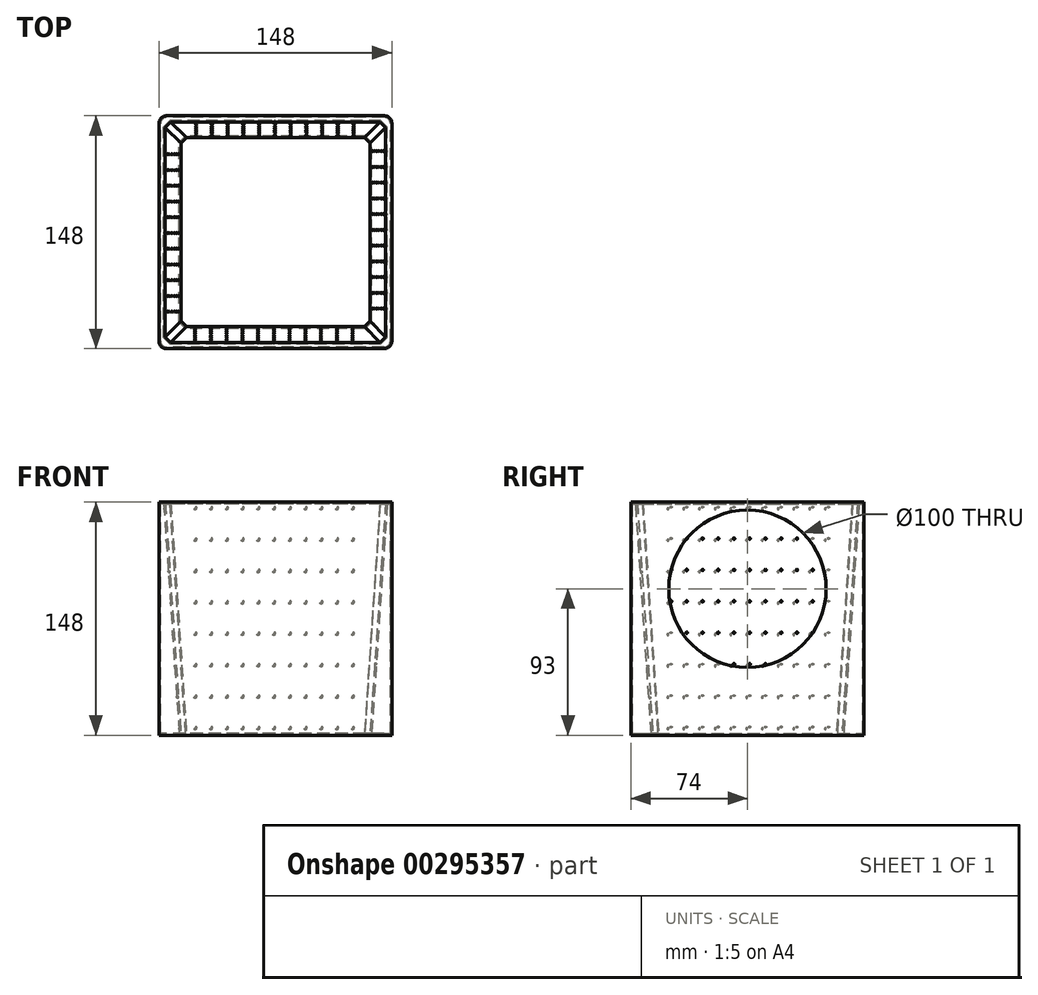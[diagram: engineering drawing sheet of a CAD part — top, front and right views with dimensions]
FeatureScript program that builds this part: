
annotation { "Feature Type Name" : "Feature", "Feature Type Description" : "" }
export const myFeature = defineFeature(function(context is Context, id is Id, definition is map)
    precondition{}
    {
        {
            var Q0;
            Q0=qCreatedBy(makeId("Top.planeOp"),FACE);
            cPlane(context, id + "F0", {"entities" : qUnion([Q0]), "cplaneType" : CPlaneType.OFFSET, "offset" : 148 * mm, "width" : 150 * mm, "height" : 150 * mm});
        }
        {
            var Q0;
            Q0=qCreatedBy(id+"F0.planeOp",FACE);
            var sketch = newSketch(context, id + "F1", { "sketchPlane" : qUnion([Q0])});
            skLineSegment(sketch, "E0.bottom", {"start": v(69, -74) * mm, "end": v(-69, -74) * mm});
            skLineSegment(sketch, "E0.top", {"start": v(69, 74) * mm, "end": v(-69, 74) * mm});
            skLineSegment(sketch, "E0.left", {"start": v(74, -69) * mm, "end": v(74, 69) * mm});
            skLineSegment(sketch, "E0.right", {"start": v(-74, -69) * mm, "end": v(-74, 69) * mm});
            skArc(sketch, "E1.filletArc", {"start": v(74, 69) * mm, "mid": v(72.54, 72.54) * mm, "end": v(69, 74) * mm});
            skArc(sketch, "E2.filletArc", {"start": v(-69, 74) * mm, "mid": v(-72.54, 72.54) * mm, "end": v(-74, 69) * mm});
            skArc(sketch, "E3.filletArc", {"start": v(-74, -69) * mm, "mid": v(-72.54, -72.54) * mm, "end": v(-69, -74) * mm});
            skArc(sketch, "E4.filletArc", {"start": v(69, -74) * mm, "mid": v(72.54, -72.54) * mm, "end": v(74, -69) * mm});
            skSolve(sketch);
        }
        {
            var Q0;
            Q0=qCreatedBy(makeId("Top.planeOp"),FACE);
            var sketch = newSketch(context, id + "F2", { "sketchPlane" : qUnion([Q0])});
            skLineSegment(sketch, "E5.bottom", {"start": v(69, -74) * mm, "end": v(-69, -74) * mm});
            skLineSegment(sketch, "E5.top", {"start": v(69, 74) * mm, "end": v(-69, 74) * mm});
            skLineSegment(sketch, "E5.left", {"start": v(74, -69) * mm, "end": v(74, 69) * mm});
            skLineSegment(sketch, "E5.right", {"start": v(-74, -69) * mm, "end": v(-74, 69) * mm});
            skArc(sketch, "E6.filletArc", {"start": v(69, -74) * mm, "mid": v(72.54, -72.54) * mm, "end": v(74, -69) * mm});
            skArc(sketch, "E7.filletArc", {"start": v(74, 69) * mm, "mid": v(72.54, 72.54) * mm, "end": v(69, 74) * mm});
            skArc(sketch, "E8.filletArc", {"start": v(-69, 74) * mm, "mid": v(-72.54, 72.54) * mm, "end": v(-74, 69) * mm});
            skArc(sketch, "E9.filletArc", {"start": v(-74, -69) * mm, "mid": v(-72.54, -72.54) * mm, "end": v(-69, -74) * mm});
            skSolve(sketch);
        }
        {
            var Q0;
            Q0=qCreatedBy(makeId("Top.planeOp"),FACE);
            var sketch = newSketch(context, id + "F3", { "sketchPlane" : qUnion([Q0])});
            skPoint(sketch, "E10.middle", {"position": v(0, 0) * mm});
            skPoint(sketch, "E11.visualSharp", {"position": v(50, -40) * mm});
            skPoint(sketch, "E12.visualSharp", {"position": v(50, 40) * mm});
            skPoint(sketch, "E13.visualSharp", {"position": v(-50, 40) * mm});
            skLineSegment(sketch, "E14.bottom", {"start": v(56.46, -60) * mm, "end": v(-56.46, -60) * mm});
            skLineSegment(sketch, "E14.top", {"start": v(56.46, 60) * mm, "end": v(-56.46, 60) * mm});
            skLineSegment(sketch, "E14.left", {"start": v(60, -56.46) * mm, "end": v(60, 56.46) * mm});
            skLineSegment(sketch, "E14.right", {"start": v(-60, -56.46) * mm, "end": v(-60, 56.46) * mm});
            skPoint(sketch, "E15.visualSharp", {"position": v(60, -60) * mm});
            skPoint(sketch, "E16.visualSharp", {"position": v(60, 60) * mm});
            skPoint(sketch, "E17.visualSharp", {"position": v(-60, 60) * mm});
            skLineSegment(sketch, "E18", {"start": v(-60, 56.46) * mm, "end": v(-56.46, 60) * mm});
            skLineSegment(sketch, "E19", {"start": v(-60, -56.46) * mm, "end": v(-56.46, -60) * mm});
            skLineSegment(sketch, "E20", {"start": v(56.46, -60) * mm, "end": v(60, -56.46) * mm});
            skLineSegment(sketch, "E21", {"start": v(60, 56.46) * mm, "end": v(56.46, 60) * mm});
            skSolve(sketch);
        }
        {
            var Q0;
            Q0=makeQuery(id+"F1.imprint","IMPRINT",FACE,{"disambiguationData":[TD([[makeQuery(id+"F1.imprint","IMPRINT",EDGE,{"derivedFrom":sQuery(id+"F1.wireOp",EDGE,"E0.bottom")}),-1.0]])]});
            var sketch = newSketch(context, id + "F4", { "sketchPlane" : qUnion([Q0])});
            skPoint(sketch, "E22.middle", {"position": v(0, 0) * mm});
            skPoint(sketch, "E23.visualSharp", {"position": v(75, 75) * mm});
            skPoint(sketch, "E24.visualSharp", {"position": v(-75, 75) * mm});
            skPoint(sketch, "E25.visualSharp", {"position": v(-75, -75) * mm});
            skPoint(sketch, "E26.visualSharp", {"position": v(75, -75) * mm});
            skLineSegment(sketch, "E27.bottom", {"start": v(66.46, -70) * mm, "end": v(-66.46, -70) * mm});
            skLineSegment(sketch, "E27.top", {"start": v(66.46, 70) * mm, "end": v(-66.46, 70) * mm});
            skLineSegment(sketch, "E27.left", {"start": v(70, -66.46) * mm, "end": v(70, 66.46) * mm});
            skLineSegment(sketch, "E27.right", {"start": v(-70, -66.46) * mm, "end": v(-70, 66.46) * mm});
            skPoint(sketch, "E28.visualSharp", {"position": v(70, 70) * mm});
            skPoint(sketch, "E29.visualSharp", {"position": v(70, -70) * mm});
            skPoint(sketch, "E30.visualSharp", {"position": v(-70, -70) * mm});
            skPoint(sketch, "E31.visualSharp", {"position": v(-70, 70) * mm});
            skLineSegment(sketch, "E32", {"start": v(-70, 66.46) * mm, "end": v(-66.46, 70) * mm});
            skLineSegment(sketch, "E33", {"start": v(-70, -66.46) * mm, "end": v(-66.46, -70) * mm});
            skLineSegment(sketch, "E34", {"start": v(66.46, -70) * mm, "end": v(70, -66.46) * mm});
            skLineSegment(sketch, "E35", {"start": v(70, 66.46) * mm, "end": v(66.46, 70) * mm});
            skSolve(sketch);
        }
        {
            var Q0;
            Q0=makeQuery(id+"F1.imprint","IMPRINT",FACE,{"disambiguationData":[TD([[makeQuery(id+"F1.imprint","IMPRINT",EDGE,{"derivedFrom":sQuery(id+"F1.wireOp",EDGE,"E0.bottom")}),-1.0]])]});
            var Q1;
            Q1=makeQuery(id+"F2.imprint","IMPRINT",FACE,{"disambiguationData":[TD([[makeQuery(id+"F2.imprint","IMPRINT",EDGE,{"derivedFrom":sQuery(id+"F2.wireOp",EDGE,"E5.bottom")}),-1.0]])]});
            loft(context, id + "F5", {"sheetProfilesArray" : [{ "sheetProfileEntities" : qUnion([Q0]) }, { "sheetProfileEntities" : qUnion([Q1]) }]});
        }
        {
            var Q1;
            Q1=makeQuery(id+"F4.imprint","IMPRINT",FACE,{"disambiguationData":[TD([[makeQuery(id+"F4.imprint","IMPRINT",EDGE,{"derivedFrom":sQuery(id+"F4.wireOp",EDGE,"E27.bottom")}),-1.0]])]});
            var Q2;
            Q2=makeQuery(id+"F3.imprint","IMPRINT",FACE,{"disambiguationData":[TD([[makeQuery(id+"F3.imprint","IMPRINT",EDGE,{"derivedFrom":sQuery(id+"F3.wireOp",EDGE,"E14.bottom")}),-1.0]])]});
            loft(context, id + "F6", {"operationType" : NewBodyOperationType.REMOVE, "sheetProfilesArray" : [{ "sheetProfileEntities" : qUnion([Q1]) }, { "sheetProfileEntities" : qUnion([Q2]) }]});
        }
        {
            var Q0;
            Q0=makeQuery(id+"F5.opLoft","CAP_FACE",FACE,{"disambiguationData":[OSD([makeQuery(id+"F1.imprint","IMPRINT",FACE,{"disambiguationData":[TD([[makeQuery(id+"F1.imprint","IMPRINT",EDGE,{"derivedFrom":sQuery(id+"F1.wireOp",EDGE,"E0.bottom")}),-1.0]])]})])],"isStart":true});
            var Q1;
            Q1=makeQuery(id+"F5.opLoft","SWEPT_BODY",BODY,{"disambiguationData":[OSD([makeQuery(id+"F1.imprint","IMPRINT",FACE,{"disambiguationData":[TD([[makeQuery(id+"F1.imprint","IMPRINT",EDGE,{"derivedFrom":sQuery(id+"F1.wireOp",EDGE,"E0.bottom")}),-1.0]])]}),makeQuery(id+"F2.imprint","IMPRINT",FACE,{"disambiguationData":[TD([[makeQuery(id+"F2.imprint","IMPRINT",EDGE,{"derivedFrom":sQuery(id+"F2.wireOp",EDGE,"E5.bottom")}),-1.0]])]})])]});
            shell(context, id + "F7", {"isHollow" : true, "entities" : qUnion([Q0]), "parts" : qUnion([Q1]), "thickness" : 1 * mm});
        }
        {
            var Q0;
            Q0=makeQuery(id+"F6.boolean.opBoolean","COPY",FACE,{"derivedFrom":makeQuery(id+"F6.opLoft","SWEPT_FACE",FACE,{"disambiguationData":[OSD([sQuery(id+"F3.wireOp",EDGE,"E14.top"),sQuery(id+"F3.wireOp",EDGE,"E16.filletArc"),sQuery(id+"F3.wireOp",EDGE,"E17.filletArc"),sQuery(id+"F4.wireOp",EDGE,"E27.top"),sQuery(id+"F4.wireOp",EDGE,"E28.filletArc"),sQuery(id+"F4.wireOp",EDGE,"E31.filletArc")])]})});
            var sketch = newSketch(context, id + "F8", { "sketchPlane" : qUnion([Q0])});
            skPoint(sketch, "E36", {"position": v(-50.4, 148.96) * mm});
            skPoint(sketch, "E37.0.1.0", {"position": v(-50.4, 128.96) * mm});
            skPoint(sketch, "E37.0.2.0", {"position": v(-50.4, 108.96) * mm});
            skPoint(sketch, "E37.0.3.0", {"position": v(-50.4, 88.96) * mm});
            skPoint(sketch, "E37.0.4.0", {"position": v(-50.4, 68.96) * mm});
            skPoint(sketch, "E37.1.0.0", {"position": v(-40.4, 148.96) * mm});
            skPoint(sketch, "E37.1.1.0", {"position": v(-40.4, 128.96) * mm});
            skPoint(sketch, "E37.1.2.0", {"position": v(-40.4, 108.96) * mm});
            skPoint(sketch, "E37.1.3.0", {"position": v(-40.4, 88.96) * mm});
            skPoint(sketch, "E37.1.4.0", {"position": v(-40.4, 68.96) * mm});
            skPoint(sketch, "E37.2.0.0", {"position": v(-30.4, 148.96) * mm});
            skPoint(sketch, "E37.2.1.0", {"position": v(-30.4, 128.96) * mm});
            skPoint(sketch, "E37.2.2.0", {"position": v(-30.4, 108.96) * mm});
            skPoint(sketch, "E37.2.3.0", {"position": v(-30.4, 88.96) * mm});
            skPoint(sketch, "E37.2.4.0", {"position": v(-30.4, 68.96) * mm});
            skPoint(sketch, "E37.3.0.0", {"position": v(-20.4, 148.96) * mm});
            skPoint(sketch, "E37.3.1.0", {"position": v(-20.4, 128.96) * mm});
            skPoint(sketch, "E37.3.2.0", {"position": v(-20.4, 108.96) * mm});
            skPoint(sketch, "E37.3.3.0", {"position": v(-20.4, 88.96) * mm});
            skPoint(sketch, "E37.3.4.0", {"position": v(-20.4, 68.96) * mm});
            skPoint(sketch, "E37.4.0.0", {"position": v(-10.4, 148.96) * mm});
            skPoint(sketch, "E37.4.1.0", {"position": v(-10.4, 128.96) * mm});
            skPoint(sketch, "E37.4.2.0", {"position": v(-10.4, 108.96) * mm});
            skPoint(sketch, "E37.4.3.0", {"position": v(-10.4, 88.96) * mm});
            skPoint(sketch, "E37.4.4.0", {"position": v(-10.4, 68.96) * mm});
            skPoint(sketch, "E37.5.0.0", {"position": v(-0.4, 148.96) * mm});
            skPoint(sketch, "E37.5.1.0", {"position": v(-0.4, 128.96) * mm});
            skPoint(sketch, "E37.5.2.0", {"position": v(-0.4, 108.96) * mm});
            skPoint(sketch, "E37.5.3.0", {"position": v(-0.4, 88.96) * mm});
            skPoint(sketch, "E37.5.4.0", {"position": v(-0.4, 68.96) * mm});
            skPoint(sketch, "E37.6.0.0", {"position": v(9.6, 148.96) * mm});
            skPoint(sketch, "E37.6.1.0", {"position": v(9.6, 128.96) * mm});
            skPoint(sketch, "E37.6.2.0", {"position": v(9.6, 108.96) * mm});
            skPoint(sketch, "E37.6.3.0", {"position": v(9.6, 88.96) * mm});
            skPoint(sketch, "E37.6.4.0", {"position": v(9.6, 68.96) * mm});
            skPoint(sketch, "E37.7.0.0", {"position": v(19.6, 148.96) * mm});
            skPoint(sketch, "E37.7.1.0", {"position": v(19.6, 128.96) * mm});
            skPoint(sketch, "E37.7.2.0", {"position": v(19.6, 108.96) * mm});
            skPoint(sketch, "E37.7.3.0", {"position": v(19.6, 88.96) * mm});
            skPoint(sketch, "E37.7.4.0", {"position": v(19.6, 68.96) * mm});
            skPoint(sketch, "E37.8.0.0", {"position": v(29.6, 148.96) * mm});
            skPoint(sketch, "E37.8.1.0", {"position": v(29.6, 128.96) * mm});
            skPoint(sketch, "E37.8.2.0", {"position": v(29.6, 108.96) * mm});
            skPoint(sketch, "E37.8.3.0", {"position": v(29.6, 88.96) * mm});
            skPoint(sketch, "E37.8.4.0", {"position": v(29.6, 68.96) * mm});
            skPoint(sketch, "E37.9.0.0", {"position": v(39.6, 148.96) * mm});
            skPoint(sketch, "E37.9.1.0", {"position": v(39.6, 128.96) * mm});
            skPoint(sketch, "E37.9.2.0", {"position": v(39.6, 108.96) * mm});
            skPoint(sketch, "E37.9.3.0", {"position": v(39.6, 88.96) * mm});
            skPoint(sketch, "E37.9.4.0", {"position": v(39.6, 68.96) * mm});
            skLineSegment(sketch, "E37.direction1", {"start": v(-50.4, 148.96) * mm, "end": v(-40.4, 148.96) * mm, "construction": true});
            skLineSegment(sketch, "E37.direction2", {"start": v(-50.4, 148.96) * mm, "end": v(-50.4, 128.96) * mm, "construction": true});
            skPoint(sketch, "E38.0.0.5", {"position": v(-50.4, 48.96) * mm});
            skPoint(sketch, "E38.0.0.6", {"position": v(-50.4, 28.96) * mm});
            skPoint(sketch, "E38.0.0.7", {"position": v(-50.4, 8.96) * mm});
            skPoint(sketch, "E38.0.1.5", {"position": v(-40.4, 48.96) * mm});
            skPoint(sketch, "E38.0.1.6", {"position": v(-40.4, 28.96) * mm});
            skPoint(sketch, "E38.0.1.7", {"position": v(-40.4, 8.96) * mm});
            skPoint(sketch, "E38.0.2.5", {"position": v(-30.4, 48.96) * mm});
            skPoint(sketch, "E38.0.2.6", {"position": v(-30.4, 28.96) * mm});
            skPoint(sketch, "E38.0.2.7", {"position": v(-30.4, 8.96) * mm});
            skPoint(sketch, "E38.0.3.5", {"position": v(-20.4, 48.96) * mm});
            skPoint(sketch, "E38.0.3.6", {"position": v(-20.4, 28.96) * mm});
            skPoint(sketch, "E38.0.3.7", {"position": v(-20.4, 8.96) * mm});
            skPoint(sketch, "E38.0.4.5", {"position": v(-10.4, 48.96) * mm});
            skPoint(sketch, "E38.0.4.6", {"position": v(-10.4, 28.96) * mm});
            skPoint(sketch, "E38.0.4.7", {"position": v(-10.4, 8.96) * mm});
            skPoint(sketch, "E38.0.5.5", {"position": v(-0.4, 48.96) * mm});
            skPoint(sketch, "E38.0.5.6", {"position": v(-0.4, 28.96) * mm});
            skPoint(sketch, "E38.0.5.7", {"position": v(-0.4, 8.96) * mm});
            skPoint(sketch, "E38.0.6.5", {"position": v(9.6, 48.96) * mm});
            skPoint(sketch, "E38.0.6.6", {"position": v(9.6, 28.96) * mm});
            skPoint(sketch, "E38.0.6.7", {"position": v(9.6, 8.96) * mm});
            skPoint(sketch, "E38.0.7.5", {"position": v(19.6, 48.96) * mm});
            skPoint(sketch, "E38.0.7.6", {"position": v(19.6, 28.96) * mm});
            skPoint(sketch, "E38.0.7.7", {"position": v(19.6, 8.96) * mm});
            skPoint(sketch, "E38.0.8.5", {"position": v(29.6, 48.96) * mm});
            skPoint(sketch, "E38.0.8.6", {"position": v(29.6, 28.96) * mm});
            skPoint(sketch, "E38.0.8.7", {"position": v(29.6, 8.96) * mm});
            skPoint(sketch, "E38.0.9.5", {"position": v(39.6, 48.96) * mm});
            skPoint(sketch, "E38.0.9.6", {"position": v(39.6, 28.96) * mm});
            skPoint(sketch, "E38.0.9.7", {"position": v(39.6, 8.96) * mm});
            skPoint(sketch, "E39.0.10.0", {"position": v(49.6, 148.96) * mm});
            skPoint(sketch, "E39.0.10.1", {"position": v(49.6, 128.96) * mm});
            skPoint(sketch, "E39.0.10.2", {"position": v(49.6, 108.96) * mm});
            skPoint(sketch, "E39.0.10.3", {"position": v(49.6, 88.96) * mm});
            skPoint(sketch, "E39.0.10.4", {"position": v(49.6, 68.96) * mm});
            skPoint(sketch, "E39.0.10.5", {"position": v(49.6, 48.96) * mm});
            skPoint(sketch, "E39.0.10.6", {"position": v(49.6, 28.96) * mm});
            skPoint(sketch, "E39.0.10.7", {"position": v(49.6, 8.96) * mm});
            skSolve(sketch);
        }
        {
            var Q0;
            Q0=sQuery(id+"F8.wireOp",VERTEX,"E36");
            var Q1;
            Q1=sQuery(id+"F8.wireOp",VERTEX,"E37.3.0.0");
            var Q2;
            Q2=sQuery(id+"F8.wireOp",VERTEX,"E37.6.1.0");
            var Q3;
            Q3=sQuery(id+"F8.wireOp",VERTEX,"E37.3.2.0");
            var Q4;
            Q4=sQuery(id+"F8.wireOp",VERTEX,"E37.6.3.0");
            var Q5;
            Q5=sQuery(id+"F8.wireOp",VERTEX,"E37.5.1.0");
            var Q6;
            Q6=sQuery(id+"F8.wireOp",VERTEX,"E37.8.2.0");
            var Q7;
            Q7=sQuery(id+"F8.wireOp",VERTEX,"E37.4.1.0");
            var Q8;
            Q8=sQuery(id+"F8.wireOp",VERTEX,"E37.7.4.0");
            var Q9;
            Q9=sQuery(id+"F8.wireOp",VERTEX,"E37.4.3.0");
            var Q10;
            Q10=sQuery(id+"F8.wireOp",VERTEX,"E37.2.2.0");
            var Q11;
            Q11=sQuery(id+"F8.wireOp",VERTEX,"E37.5.3.0");
            var Q12;
            Q12=sQuery(id+"F8.wireOp",VERTEX,"E37.2.4.0");
            var Q13;
            Q13=sQuery(id+"F8.wireOp",VERTEX,"E37.6.0.0");
            var Q14;
            Q14=sQuery(id+"F8.wireOp",VERTEX,"E37.7.0.0");
            var Q15;
            Q15=sQuery(id+"F8.wireOp",VERTEX,"E37.3.4.0");
            var Q16;
            Q16=sQuery(id+"F8.wireOp",VERTEX,"E37.7.2.0");
            var Q17;
            Q17=sQuery(id+"F8.wireOp",VERTEX,"E37.3.1.0");
            var Q18;
            Q18=sQuery(id+"F8.wireOp",VERTEX,"E37.5.0.0");
            var Q19;
            Q19=sQuery(id+"F8.wireOp",VERTEX,"E37.6.2.0");
            var Q20;
            Q20=sQuery(id+"F8.wireOp",VERTEX,"E37.8.1.0");
            var Q21;
            Q21=sQuery(id+"F8.wireOp",VERTEX,"E37.3.3.0");
            var Q22;
            Q22=sQuery(id+"F8.wireOp",VERTEX,"E37.6.4.0");
            var Q23;
            Q23=sQuery(id+"F8.wireOp",VERTEX,"E37.5.2.0");
            var Q24;
            Q24=sQuery(id+"F8.wireOp",VERTEX,"E37.1.2.0");
            var Q25;
            Q25=sQuery(id+"F8.wireOp",VERTEX,"E37.1.1.0");
            var Q26;
            Q26=sQuery(id+"F8.wireOp",VERTEX,"E37.1.0.0");
            var Q27;
            Q27=sQuery(id+"F8.wireOp",VERTEX,"E37.7.3.0");
            var Q28;
            Q28=sQuery(id+"F8.wireOp",VERTEX,"E37.4.2.0");
            var Q29;
            Q29=sQuery(id+"F8.wireOp",VERTEX,"E37.8.0.0");
            var Q30;
            Q30=sQuery(id+"F8.wireOp",VERTEX,"E37.4.4.0");
            var Q31;
            Q31=sQuery(id+"F8.wireOp",VERTEX,"E37.2.3.0");
            var Q32;
            Q32=sQuery(id+"F8.wireOp",VERTEX,"E37.5.4.0");
            var Q33;
            Q33=sQuery(id+"F8.wireOp",VERTEX,"E37.9.0.0");
            var Q34;
            Q34=sQuery(id+"F8.wireOp",VERTEX,"E37.2.1.0");
            var Q35;
            Q35=sQuery(id+"F8.wireOp",VERTEX,"E37.2.0.0");
            var Q36;
            Q36=sQuery(id+"F8.wireOp",VERTEX,"E37.7.1.0");
            var Q37;
            Q37=sQuery(id+"F8.wireOp",VERTEX,"E37.4.0.0");
            var Q38;
            Q38=sQuery(id+"F8.wireOp",VERTEX,"E37.9.4.0");
            var Q39;
            Q39=sQuery(id+"F8.wireOp",VERTEX,"E39.0.10.6");
            var Q40;
            Q40=sQuery(id+"F8.wireOp",VERTEX,"E39.0.10.3");
            var Q41;
            Q41=sQuery(id+"F8.wireOp",VERTEX,"E38.0.5.6");
            var Q42;
            Q42=sQuery(id+"F8.wireOp",VERTEX,"E38.0.8.6");
            var Q43;
            Q43=sQuery(id+"F8.wireOp",VERTEX,"E38.0.9.6");
            var Q44;
            Q44=sQuery(id+"F8.wireOp",VERTEX,"E38.0.0.6");
            var Q45;
            Q45=sQuery(id+"F8.wireOp",VERTEX,"E39.0.10.5");
            var Q46;
            Q46=sQuery(id+"F8.wireOp",VERTEX,"E38.0.4.7");
            var Q47;
            Q47=sQuery(id+"F8.wireOp",VERTEX,"E38.0.7.5");
            var Q48;
            Q48=sQuery(id+"F8.wireOp",VERTEX,"E38.0.5.7");
            var Q49;
            Q49=sQuery(id+"F8.wireOp",VERTEX,"E38.0.8.7");
            var Q50;
            Q50=sQuery(id+"F8.wireOp",VERTEX,"E38.0.3.6");
            var Q51;
            Q51=sQuery(id+"F8.wireOp",VERTEX,"E39.0.10.2");
            var Q52;
            Q52=sQuery(id+"F8.wireOp",VERTEX,"E37.0.3.0");
            var Q53;
            Q53=sQuery(id+"F8.wireOp",VERTEX,"E37.9.3.0");
            var Q54;
            Q54=sQuery(id+"F8.wireOp",VERTEX,"E39.0.10.0");
            var Q55;
            Q55=sQuery(id+"F8.wireOp",VERTEX,"E38.0.9.5");
            var Q56;
            Q56=sQuery(id+"F8.wireOp",VERTEX,"E38.0.7.6");
            var Q57;
            Q57=sQuery(id+"F8.wireOp",VERTEX,"E38.0.7.7");
            var Q58;
            Q58=sQuery(id+"F8.wireOp",VERTEX,"E38.0.3.7");
            var Q59;
            Q59=sQuery(id+"F8.wireOp",VERTEX,"E37.9.1.0");
            var Q60;
            Q60=sQuery(id+"F8.wireOp",VERTEX,"E38.0.0.5");
            var Q61;
            Q61=sQuery(id+"F8.wireOp",VERTEX,"E39.0.10.1");
            var Q62;
            Q62=sQuery(id+"F8.wireOp",VERTEX,"E38.0.2.7");
            var Q63;
            Q63=sQuery(id+"F8.wireOp",VERTEX,"E37.0.2.0");
            var Q64;
            Q64=sQuery(id+"F8.wireOp",VERTEX,"E37.0.1.0");
            var Q65;
            Q65=sQuery(id+"F8.wireOp",VERTEX,"E39.0.10.7");
            var Q66;
            Q66=sQuery(id+"F8.wireOp",VERTEX,"E37.1.4.0");
            var Q67;
            Q67=sQuery(id+"F8.wireOp",VERTEX,"E38.0.8.5");
            var Q68;
            Q68=sQuery(id+"F8.wireOp",VERTEX,"E38.0.5.5");
            var Q69;
            Q69=sQuery(id+"F8.wireOp",VERTEX,"E37.9.2.0");
            var Q70;
            Q70=sQuery(id+"F8.wireOp",VERTEX,"E38.0.4.6");
            var Q71;
            Q71=sQuery(id+"F8.wireOp",VERTEX,"E37.8.3.0");
            var Q72;
            Q72=sQuery(id+"F8.wireOp",VERTEX,"E37.0.4.0");
            var Q73;
            Q73=sQuery(id+"F8.wireOp",VERTEX,"E38.0.0.7");
            var Q74;
            Q74=sQuery(id+"F8.wireOp",VERTEX,"E39.0.10.4");
            var Q75;
            Q75=sQuery(id+"F8.wireOp",VERTEX,"E38.0.1.6");
            var Q76;
            Q76=sQuery(id+"F8.wireOp",VERTEX,"E38.0.9.7");
            var Q77;
            Q77=sQuery(id+"F8.wireOp",VERTEX,"E37.8.4.0");
            var Q78;
            Q78=sQuery(id+"F8.wireOp",VERTEX,"E38.0.2.6");
            var Q79;
            Q79=sQuery(id+"F8.wireOp",VERTEX,"E37.1.3.0");
            var Q80;
            Q80=sQuery(id+"F8.wireOp",VERTEX,"E38.0.3.5");
            var Q81;
            Q81=sQuery(id+"F8.wireOp",VERTEX,"E38.0.1.5");
            var Q82;
            Q82=sQuery(id+"F8.wireOp",VERTEX,"E38.0.6.6");
            var Q83;
            Q83=sQuery(id+"F8.wireOp",VERTEX,"E38.0.1.7");
            var Q84;
            Q84=sQuery(id+"F8.wireOp",VERTEX,"E38.0.6.5");
            var Q85;
            Q85=sQuery(id+"F8.wireOp",VERTEX,"E38.0.4.5");
            var Q86;
            Q86=sQuery(id+"F8.wireOp",VERTEX,"E38.0.6.7");
            var Q87;
            Q87=sQuery(id+"F8.wireOp",VERTEX,"E38.0.2.5");
            var Q88;
            Q88=makeQuery(id+"F5.opLoft","SWEPT_BODY",BODY,{"disambiguationData":[OSD([makeQuery(id+"F1.imprint","IMPRINT",FACE,{"disambiguationData":[TD([[makeQuery(id+"F1.imprint","IMPRINT",EDGE,{"derivedFrom":sQuery(id+"F1.wireOp",EDGE,"E0.bottom")}),-1.0]])]}),makeQuery(id+"F2.imprint","IMPRINT",FACE,{"disambiguationData":[TD([[makeQuery(id+"F2.imprint","IMPRINT",EDGE,{"derivedFrom":sQuery(id+"F2.wireOp",EDGE,"E5.bottom")}),-1.0]])]})])]});
            hole(context, id + "F9", {"style" : HoleStyle.SIMPLE, "endStyle" : HoleEndStyle.BLIND, "holeDiameter" : 1 * mm, "holeDepth" : 1 * mm, "tappedDepth" : 12 * mm, "tapClearance" : 3, "locations" : qUnion([Q0, Q1, Q2, Q3, Q4, Q5, Q6, Q7, Q8, Q9, Q10, Q11, Q12, Q13, Q14, Q15, Q16, Q17, Q18, Q19, Q20, Q21, Q22, Q23, Q24, Q25, Q26, Q27, Q28, Q29, Q30, Q31, Q32, Q33, Q34, Q35, Q36, Q37, Q38, Q39, Q40, Q41, Q42, Q43, Q44, Q45, Q46, Q47, Q48, Q49, Q50, Q51, Q52, Q53, Q54, Q55, Q56, Q57, Q58, Q59, Q60, Q61, Q62, Q63, Q64, Q65, Q66, Q67, Q68, Q69, Q70, Q71, Q72, Q73, Q74, Q75, Q76, Q77, Q78, Q79, Q80, Q81, Q82, Q83, Q84, Q85, Q86, Q87]), "scope" : qUnion([Q88])});
        }
        {
            var Q0;
            Q0=makeQuery(id+"F6.boolean.opBoolean","COPY",FACE,{"derivedFrom":makeQuery(id+"F6.opLoft","SWEPT_FACE",FACE,{"disambiguationData":[OSD([sQuery(id+"F3.wireOp",EDGE,"E14.right"),sQuery(id+"F3.wireOp",EDGE,"E18"),sQuery(id+"F3.wireOp",EDGE,"E19"),sQuery(id+"F4.wireOp",EDGE,"E27.right"),sQuery(id+"F4.wireOp",EDGE,"E32"),sQuery(id+"F4.wireOp",EDGE,"E33")])]})});
            var sketch = newSketch(context, id + "F10", { "sketchPlane" : qUnion([Q0])});
            skPoint(sketch, "E40", {"position": v(-50.5, 148.2) * mm});
            skPoint(sketch, "E41.0.1.0", {"position": v(-50.5, 128.2) * mm});
            skPoint(sketch, "E41.0.2.0", {"position": v(-50.5, 108.2) * mm});
            skPoint(sketch, "E41.0.3.0", {"position": v(-50.5, 88.2) * mm});
            skPoint(sketch, "E41.0.4.0", {"position": v(-50.5, 68.2) * mm});
            skPoint(sketch, "E41.1.0.0", {"position": v(-40.5, 148.2) * mm});
            skPoint(sketch, "E41.1.1.0", {"position": v(-40.5, 128.2) * mm});
            skPoint(sketch, "E41.1.2.0", {"position": v(-40.5, 108.2) * mm});
            skPoint(sketch, "E41.1.3.0", {"position": v(-40.5, 88.2) * mm});
            skPoint(sketch, "E41.1.4.0", {"position": v(-40.5, 68.2) * mm});
            skPoint(sketch, "E41.2.0.0", {"position": v(-30.5, 148.2) * mm});
            skPoint(sketch, "E41.2.1.0", {"position": v(-30.5, 128.2) * mm});
            skPoint(sketch, "E41.2.2.0", {"position": v(-30.5, 108.2) * mm});
            skPoint(sketch, "E41.2.3.0", {"position": v(-30.5, 88.2) * mm});
            skPoint(sketch, "E41.2.4.0", {"position": v(-30.5, 68.2) * mm});
            skPoint(sketch, "E41.3.0.0", {"position": v(-20.5, 148.2) * mm});
            skPoint(sketch, "E41.3.1.0", {"position": v(-20.5, 128.2) * mm});
            skPoint(sketch, "E41.3.2.0", {"position": v(-20.5, 108.2) * mm});
            skPoint(sketch, "E41.3.3.0", {"position": v(-20.5, 88.2) * mm});
            skPoint(sketch, "E41.3.4.0", {"position": v(-20.5, 68.2) * mm});
            skPoint(sketch, "E41.4.0.0", {"position": v(-10.5, 148.2) * mm});
            skPoint(sketch, "E41.4.1.0", {"position": v(-10.5, 128.2) * mm});
            skPoint(sketch, "E41.4.2.0", {"position": v(-10.5, 108.2) * mm});
            skPoint(sketch, "E41.4.3.0", {"position": v(-10.5, 88.2) * mm});
            skPoint(sketch, "E41.4.4.0", {"position": v(-10.5, 68.2) * mm});
            skPoint(sketch, "E41.5.0.0", {"position": v(-0.5, 148.2) * mm});
            skPoint(sketch, "E41.5.1.0", {"position": v(-0.5, 128.2) * mm});
            skPoint(sketch, "E41.5.2.0", {"position": v(-0.5, 108.2) * mm});
            skPoint(sketch, "E41.5.3.0", {"position": v(-0.5, 88.2) * mm});
            skPoint(sketch, "E41.5.4.0", {"position": v(-0.5, 68.2) * mm});
            skPoint(sketch, "E41.6.0.0", {"position": v(9.5, 148.2) * mm});
            skPoint(sketch, "E41.6.1.0", {"position": v(9.5, 128.2) * mm});
            skPoint(sketch, "E41.6.2.0", {"position": v(9.5, 108.2) * mm});
            skPoint(sketch, "E41.6.3.0", {"position": v(9.5, 88.2) * mm});
            skPoint(sketch, "E41.6.4.0", {"position": v(9.5, 68.2) * mm});
            skPoint(sketch, "E41.7.0.0", {"position": v(19.5, 148.2) * mm});
            skPoint(sketch, "E41.7.1.0", {"position": v(19.5, 128.2) * mm});
            skPoint(sketch, "E41.7.2.0", {"position": v(19.5, 108.2) * mm});
            skPoint(sketch, "E41.7.3.0", {"position": v(19.5, 88.2) * mm});
            skPoint(sketch, "E41.7.4.0", {"position": v(19.5, 68.2) * mm});
            skPoint(sketch, "E41.8.0.0", {"position": v(29.5, 148.2) * mm});
            skPoint(sketch, "E41.8.1.0", {"position": v(29.5, 128.2) * mm});
            skPoint(sketch, "E41.8.2.0", {"position": v(29.5, 108.2) * mm});
            skPoint(sketch, "E41.8.3.0", {"position": v(29.5, 88.2) * mm});
            skPoint(sketch, "E41.8.4.0", {"position": v(29.5, 68.2) * mm});
            skPoint(sketch, "E41.9.0.0", {"position": v(39.5, 148.2) * mm});
            skPoint(sketch, "E41.9.1.0", {"position": v(39.5, 128.2) * mm});
            skPoint(sketch, "E41.9.2.0", {"position": v(39.5, 108.2) * mm});
            skPoint(sketch, "E41.9.3.0", {"position": v(39.5, 88.2) * mm});
            skPoint(sketch, "E41.9.4.0", {"position": v(39.5, 68.2) * mm});
            skLineSegment(sketch, "E41.direction1", {"start": v(-50.5, 148.2) * mm, "end": v(-40.5, 148.2) * mm, "construction": true});
            skLineSegment(sketch, "E41.direction2", {"start": v(-50.5, 148.2) * mm, "end": v(-50.5, 128.2) * mm, "construction": true});
            skPoint(sketch, "E42.0.0.5", {"position": v(-50.5, 48.2) * mm});
            skPoint(sketch, "E42.0.0.6", {"position": v(-50.5, 28.2) * mm});
            skPoint(sketch, "E42.0.0.7", {"position": v(-50.5, 8.2) * mm});
            skPoint(sketch, "E42.0.1.5", {"position": v(-40.5, 48.2) * mm});
            skPoint(sketch, "E42.0.1.6", {"position": v(-40.5, 28.2) * mm});
            skPoint(sketch, "E42.0.1.7", {"position": v(-40.5, 8.2) * mm});
            skPoint(sketch, "E42.0.2.5", {"position": v(-30.5, 48.2) * mm});
            skPoint(sketch, "E42.0.2.6", {"position": v(-30.5, 28.2) * mm});
            skPoint(sketch, "E42.0.2.7", {"position": v(-30.5, 8.2) * mm});
            skPoint(sketch, "E42.0.3.5", {"position": v(-20.5, 48.2) * mm});
            skPoint(sketch, "E42.0.3.6", {"position": v(-20.5, 28.2) * mm});
            skPoint(sketch, "E42.0.3.7", {"position": v(-20.5, 8.2) * mm});
            skPoint(sketch, "E42.0.4.5", {"position": v(-10.5, 48.2) * mm});
            skPoint(sketch, "E42.0.4.6", {"position": v(-10.5, 28.2) * mm});
            skPoint(sketch, "E42.0.4.7", {"position": v(-10.5, 8.2) * mm});
            skPoint(sketch, "E42.0.5.5", {"position": v(-0.5, 48.2) * mm});
            skPoint(sketch, "E42.0.5.6", {"position": v(-0.5, 28.2) * mm});
            skPoint(sketch, "E42.0.5.7", {"position": v(-0.5, 8.2) * mm});
            skPoint(sketch, "E42.0.6.5", {"position": v(9.5, 48.2) * mm});
            skPoint(sketch, "E42.0.6.6", {"position": v(9.5, 28.2) * mm});
            skPoint(sketch, "E42.0.6.7", {"position": v(9.5, 8.2) * mm});
            skPoint(sketch, "E42.0.7.5", {"position": v(19.5, 48.2) * mm});
            skPoint(sketch, "E42.0.7.6", {"position": v(19.5, 28.2) * mm});
            skPoint(sketch, "E42.0.7.7", {"position": v(19.5, 8.2) * mm});
            skPoint(sketch, "E42.0.8.5", {"position": v(29.5, 48.2) * mm});
            skPoint(sketch, "E42.0.8.6", {"position": v(29.5, 28.2) * mm});
            skPoint(sketch, "E42.0.8.7", {"position": v(29.5, 8.2) * mm});
            skPoint(sketch, "E42.0.9.5", {"position": v(39.5, 48.2) * mm});
            skPoint(sketch, "E42.0.9.6", {"position": v(39.5, 28.2) * mm});
            skPoint(sketch, "E42.0.9.7", {"position": v(39.5, 8.2) * mm});
            skPoint(sketch, "E43.0.10.0", {"position": v(49.5, 148.2) * mm});
            skPoint(sketch, "E43.0.10.1", {"position": v(49.5, 128.2) * mm});
            skPoint(sketch, "E43.0.10.2", {"position": v(49.5, 108.2) * mm});
            skPoint(sketch, "E43.0.10.3", {"position": v(49.5, 88.2) * mm});
            skPoint(sketch, "E43.0.10.4", {"position": v(49.5, 68.2) * mm});
            skPoint(sketch, "E43.0.10.5", {"position": v(49.5, 48.2) * mm});
            skPoint(sketch, "E43.0.10.6", {"position": v(49.5, 28.2) * mm});
            skPoint(sketch, "E43.0.10.7", {"position": v(49.5, 8.2) * mm});
            skSolve(sketch);
        }
        {
            var Q0;
            Q0=makeQuery(id+"F6.boolean.opBoolean","COPY",FACE,{"derivedFrom":makeQuery(id+"F6.opLoft","SWEPT_FACE",FACE,{"disambiguationData":[OSD([sQuery(id+"F3.wireOp",EDGE,"E14.bottom"),sQuery(id+"F3.wireOp",EDGE,"E19"),sQuery(id+"F3.wireOp",EDGE,"E20"),sQuery(id+"F4.wireOp",EDGE,"E27.bottom"),sQuery(id+"F4.wireOp",EDGE,"E33"),sQuery(id+"F4.wireOp",EDGE,"E34")])]})});
            var sketch = newSketch(context, id + "F11", { "sketchPlane" : qUnion([Q0])});
            skPoint(sketch, "E44", {"position": v(-49, 148) * mm});
            skPoint(sketch, "E45.0.1.0", {"position": v(-49, 128) * mm});
            skPoint(sketch, "E45.0.2.0", {"position": v(-49, 108) * mm});
            skPoint(sketch, "E45.0.3.0", {"position": v(-49, 88) * mm});
            skPoint(sketch, "E45.0.4.0", {"position": v(-49, 68) * mm});
            skPoint(sketch, "E45.1.0.0", {"position": v(-39, 148) * mm});
            skPoint(sketch, "E45.1.1.0", {"position": v(-39, 128) * mm});
            skPoint(sketch, "E45.1.2.0", {"position": v(-39, 108) * mm});
            skPoint(sketch, "E45.1.3.0", {"position": v(-39, 88) * mm});
            skPoint(sketch, "E45.1.4.0", {"position": v(-39, 68) * mm});
            skPoint(sketch, "E45.2.0.0", {"position": v(-29, 148) * mm});
            skPoint(sketch, "E45.2.1.0", {"position": v(-29, 128) * mm});
            skPoint(sketch, "E45.2.2.0", {"position": v(-29, 108) * mm});
            skPoint(sketch, "E45.2.3.0", {"position": v(-29, 88) * mm});
            skPoint(sketch, "E45.2.4.0", {"position": v(-29, 68) * mm});
            skPoint(sketch, "E45.3.0.0", {"position": v(-19, 148) * mm});
            skPoint(sketch, "E45.3.1.0", {"position": v(-19, 128) * mm});
            skPoint(sketch, "E45.3.2.0", {"position": v(-19, 108) * mm});
            skPoint(sketch, "E45.3.3.0", {"position": v(-19, 88) * mm});
            skPoint(sketch, "E45.3.4.0", {"position": v(-19, 68) * mm});
            skPoint(sketch, "E45.4.0.0", {"position": v(-9, 148) * mm});
            skPoint(sketch, "E45.4.1.0", {"position": v(-9, 128) * mm});
            skPoint(sketch, "E45.4.2.0", {"position": v(-9, 108) * mm});
            skPoint(sketch, "E45.4.3.0", {"position": v(-9, 88) * mm});
            skPoint(sketch, "E45.4.4.0", {"position": v(-9, 68) * mm});
            skPoint(sketch, "E45.5.0.0", {"position": v(1, 148) * mm});
            skPoint(sketch, "E45.5.1.0", {"position": v(1, 128) * mm});
            skPoint(sketch, "E45.5.2.0", {"position": v(1, 108) * mm});
            skPoint(sketch, "E45.5.3.0", {"position": v(1, 88) * mm});
            skPoint(sketch, "E45.5.4.0", {"position": v(1, 68) * mm});
            skPoint(sketch, "E45.6.0.0", {"position": v(11, 148) * mm});
            skPoint(sketch, "E45.6.1.0", {"position": v(11, 128) * mm});
            skPoint(sketch, "E45.6.2.0", {"position": v(11, 108) * mm});
            skPoint(sketch, "E45.6.3.0", {"position": v(11, 88) * mm});
            skPoint(sketch, "E45.6.4.0", {"position": v(11, 68) * mm});
            skPoint(sketch, "E45.7.0.0", {"position": v(21, 148) * mm});
            skPoint(sketch, "E45.7.1.0", {"position": v(21, 128) * mm});
            skPoint(sketch, "E45.7.2.0", {"position": v(21, 108) * mm});
            skPoint(sketch, "E45.7.3.0", {"position": v(21, 88) * mm});
            skPoint(sketch, "E45.7.4.0", {"position": v(21, 68) * mm});
            skPoint(sketch, "E45.8.0.0", {"position": v(31, 148) * mm});
            skPoint(sketch, "E45.8.1.0", {"position": v(31, 128) * mm});
            skPoint(sketch, "E45.8.2.0", {"position": v(31, 108) * mm});
            skPoint(sketch, "E45.8.3.0", {"position": v(31, 88) * mm});
            skPoint(sketch, "E45.8.4.0", {"position": v(31, 68) * mm});
            skPoint(sketch, "E45.9.0.0", {"position": v(41, 148) * mm});
            skPoint(sketch, "E45.9.1.0", {"position": v(41, 128) * mm});
            skPoint(sketch, "E45.9.2.0", {"position": v(41, 108) * mm});
            skPoint(sketch, "E45.9.3.0", {"position": v(41, 88) * mm});
            skPoint(sketch, "E45.9.4.0", {"position": v(41, 68) * mm});
            skLineSegment(sketch, "E45.direction1", {"start": v(-49, 148) * mm, "end": v(-39, 148) * mm, "construction": true});
            skLineSegment(sketch, "E45.direction2", {"start": v(-49, 148) * mm, "end": v(-49, 128) * mm, "construction": true});
            skPoint(sketch, "E46.0.0.5", {"position": v(-49, 48) * mm});
            skPoint(sketch, "E46.0.0.6", {"position": v(-49, 28) * mm});
            skPoint(sketch, "E46.0.0.7", {"position": v(-49, 8) * mm});
            skPoint(sketch, "E46.0.1.5", {"position": v(-39, 48) * mm});
            skPoint(sketch, "E46.0.1.6", {"position": v(-39, 28) * mm});
            skPoint(sketch, "E46.0.1.7", {"position": v(-39, 8) * mm});
            skPoint(sketch, "E46.0.2.5", {"position": v(-29, 48) * mm});
            skPoint(sketch, "E46.0.2.6", {"position": v(-29, 28) * mm});
            skPoint(sketch, "E46.0.2.7", {"position": v(-29, 8) * mm});
            skPoint(sketch, "E46.0.3.5", {"position": v(-19, 48) * mm});
            skPoint(sketch, "E46.0.3.6", {"position": v(-19, 28) * mm});
            skPoint(sketch, "E46.0.3.7", {"position": v(-19, 8) * mm});
            skPoint(sketch, "E46.0.4.5", {"position": v(-9, 48) * mm});
            skPoint(sketch, "E46.0.4.6", {"position": v(-9, 28) * mm});
            skPoint(sketch, "E46.0.4.7", {"position": v(-9, 8) * mm});
            skPoint(sketch, "E46.0.5.5", {"position": v(1, 48) * mm});
            skPoint(sketch, "E46.0.5.6", {"position": v(1, 28) * mm});
            skPoint(sketch, "E46.0.5.7", {"position": v(1, 8) * mm});
            skPoint(sketch, "E46.0.6.5", {"position": v(11, 48) * mm});
            skPoint(sketch, "E46.0.6.6", {"position": v(11, 28) * mm});
            skPoint(sketch, "E46.0.6.7", {"position": v(11, 8) * mm});
            skPoint(sketch, "E46.0.7.5", {"position": v(21, 48) * mm});
            skPoint(sketch, "E46.0.7.6", {"position": v(21, 28) * mm});
            skPoint(sketch, "E46.0.7.7", {"position": v(21, 8) * mm});
            skPoint(sketch, "E46.0.8.5", {"position": v(31, 48) * mm});
            skPoint(sketch, "E46.0.8.6", {"position": v(31, 28) * mm});
            skPoint(sketch, "E46.0.8.7", {"position": v(31, 8) * mm});
            skPoint(sketch, "E46.0.9.5", {"position": v(41, 48) * mm});
            skPoint(sketch, "E46.0.9.6", {"position": v(41, 28) * mm});
            skPoint(sketch, "E46.0.9.7", {"position": v(41, 8) * mm});
            skPoint(sketch, "E47.0.10.0", {"position": v(51, 148) * mm});
            skPoint(sketch, "E47.0.10.1", {"position": v(51, 128) * mm});
            skPoint(sketch, "E47.0.10.2", {"position": v(51, 108) * mm});
            skPoint(sketch, "E47.0.10.3", {"position": v(51, 88) * mm});
            skPoint(sketch, "E47.0.10.4", {"position": v(51, 68) * mm});
            skPoint(sketch, "E47.0.10.5", {"position": v(51, 48) * mm});
            skPoint(sketch, "E47.0.10.6", {"position": v(51, 28) * mm});
            skPoint(sketch, "E47.0.10.7", {"position": v(51, 8) * mm});
            skSolve(sketch);
        }
        {
            var Q0;
            Q0=makeQuery(id+"F5.opLoft","SWEPT_FACE",FACE,{"disambiguationData":[OSD([sQuery(id+"F1.wireOp",EDGE,"E0.left"),sQuery(id+"F1.wireOp",EDGE,"E1.filletArc"),sQuery(id+"F1.wireOp",EDGE,"E4.filletArc"),sQuery(id+"F2.wireOp",EDGE,"E5.left"),sQuery(id+"F2.wireOp",EDGE,"E6.filletArc"),sQuery(id+"F2.wireOp",EDGE,"E7.filletArc")])]});
            var sketch = newSketch(context, id + "F12", { "sketchPlane" : qUnion([Q0])});
            skCircle(sketch, "E48", {"center": v(0, 93) * mm, "radius": 50 * mm});
            skSolve(sketch);
        }
        {
            var Q0;
            Q0=qSketchRegion(id+"F12",true);
            extrude(context, id + "F13", {"entities" : qUnion([Q0]), "operationType" : NewBodyOperationType.REMOVE, "oppositeDirection" : true, "depth" : 2 * mm});
        }
        {
            var Q0;
            Q0=makeQuery(id+"F6.boolean.opBoolean","COPY",FACE,{"derivedFrom":makeQuery(id+"F6.opLoft","SWEPT_FACE",FACE,{"disambiguationData":[OSD([sQuery(id+"F3.wireOp",EDGE,"E14.left"),sQuery(id+"F3.wireOp",EDGE,"E20"),sQuery(id+"F3.wireOp",EDGE,"E21"),sQuery(id+"F4.wireOp",EDGE,"E27.left"),sQuery(id+"F4.wireOp",EDGE,"E34"),sQuery(id+"F4.wireOp",EDGE,"E35")])]})});
            var sketch = newSketch(context, id + "F14", { "sketchPlane" : qUnion([Q0])});
            skPoint(sketch, "E49", {"position": v(-51.44, 149.32) * mm});
            skPoint(sketch, "E50.0.1.0", {"position": v(-51.44, 129.32) * mm});
            skPoint(sketch, "E50.0.2.0", {"position": v(-51.44, 109.32) * mm});
            skPoint(sketch, "E50.0.3.0", {"position": v(-51.44, 89.32) * mm});
            skPoint(sketch, "E50.0.4.0", {"position": v(-51.44, 69.32) * mm});
            skPoint(sketch, "E50.1.0.0", {"position": v(-41.44, 149.32) * mm});
            skPoint(sketch, "E50.1.1.0", {"position": v(-41.44, 129.32) * mm});
            skPoint(sketch, "E50.1.2.0", {"position": v(-41.44, 109.32) * mm});
            skPoint(sketch, "E50.1.3.0", {"position": v(-41.44, 89.32) * mm});
            skPoint(sketch, "E50.1.4.0", {"position": v(-41.44, 69.32) * mm});
            skPoint(sketch, "E50.2.0.0", {"position": v(-31.44, 149.32) * mm});
            skPoint(sketch, "E50.2.1.0", {"position": v(-31.44, 129.32) * mm});
            skPoint(sketch, "E50.2.2.0", {"position": v(-31.44, 109.32) * mm});
            skPoint(sketch, "E50.2.3.0", {"position": v(-31.44, 89.32) * mm});
            skPoint(sketch, "E50.2.4.0", {"position": v(-31.44, 69.32) * mm});
            skPoint(sketch, "E50.3.0.0", {"position": v(-21.44, 149.32) * mm});
            skPoint(sketch, "E50.3.1.0", {"position": v(-21.44, 129.32) * mm});
            skPoint(sketch, "E50.3.2.0", {"position": v(-21.44, 109.32) * mm});
            skPoint(sketch, "E50.3.3.0", {"position": v(-21.44, 89.32) * mm});
            skPoint(sketch, "E50.3.4.0", {"position": v(-21.44, 69.32) * mm});
            skPoint(sketch, "E50.4.0.0", {"position": v(-11.44, 149.32) * mm});
            skPoint(sketch, "E50.4.1.0", {"position": v(-11.44, 129.32) * mm});
            skPoint(sketch, "E50.4.2.0", {"position": v(-11.44, 109.32) * mm});
            skPoint(sketch, "E50.4.3.0", {"position": v(-11.44, 89.32) * mm});
            skPoint(sketch, "E50.4.4.0", {"position": v(-11.44, 69.32) * mm});
            skPoint(sketch, "E50.5.0.0", {"position": v(-1.44, 149.32) * mm});
            skPoint(sketch, "E50.5.1.0", {"position": v(-1.44, 129.32) * mm});
            skPoint(sketch, "E50.5.2.0", {"position": v(-1.44, 109.32) * mm});
            skPoint(sketch, "E50.5.3.0", {"position": v(-1.44, 89.32) * mm});
            skPoint(sketch, "E50.5.4.0", {"position": v(-1.44, 69.32) * mm});
            skPoint(sketch, "E50.6.0.0", {"position": v(8.56, 149.32) * mm});
            skPoint(sketch, "E50.6.1.0", {"position": v(8.56, 129.32) * mm});
            skPoint(sketch, "E50.6.2.0", {"position": v(8.56, 109.32) * mm});
            skPoint(sketch, "E50.6.3.0", {"position": v(8.56, 89.32) * mm});
            skPoint(sketch, "E50.6.4.0", {"position": v(8.56, 69.32) * mm});
            skPoint(sketch, "E50.7.0.0", {"position": v(18.56, 149.32) * mm});
            skPoint(sketch, "E50.7.1.0", {"position": v(18.56, 129.32) * mm});
            skPoint(sketch, "E50.7.2.0", {"position": v(18.56, 109.32) * mm});
            skPoint(sketch, "E50.7.3.0", {"position": v(18.56, 89.32) * mm});
            skPoint(sketch, "E50.7.4.0", {"position": v(18.56, 69.32) * mm});
            skPoint(sketch, "E50.8.0.0", {"position": v(28.56, 149.32) * mm});
            skPoint(sketch, "E50.8.1.0", {"position": v(28.56, 129.32) * mm});
            skPoint(sketch, "E50.8.2.0", {"position": v(28.56, 109.32) * mm});
            skPoint(sketch, "E50.8.3.0", {"position": v(28.56, 89.32) * mm});
            skPoint(sketch, "E50.8.4.0", {"position": v(28.56, 69.32) * mm});
            skPoint(sketch, "E50.9.0.0", {"position": v(38.56, 149.32) * mm});
            skPoint(sketch, "E50.9.1.0", {"position": v(38.56, 129.32) * mm});
            skPoint(sketch, "E50.9.2.0", {"position": v(38.56, 109.32) * mm});
            skPoint(sketch, "E50.9.3.0", {"position": v(38.56, 89.32) * mm});
            skPoint(sketch, "E50.9.4.0", {"position": v(38.56, 69.32) * mm});
            skLineSegment(sketch, "E50.direction1", {"start": v(-51.44, 149.32) * mm, "end": v(-41.44, 149.32) * mm, "construction": true});
            skLineSegment(sketch, "E50.direction2", {"start": v(-51.44, 149.32) * mm, "end": v(-51.44, 129.32) * mm, "construction": true});
            skPoint(sketch, "E51.0.0.5", {"position": v(-51.44, 49.32) * mm});
            skPoint(sketch, "E51.0.0.6", {"position": v(-51.44, 29.32) * mm});
            skPoint(sketch, "E51.0.0.7", {"position": v(-51.44, 9.32) * mm});
            skPoint(sketch, "E51.0.1.5", {"position": v(-41.44, 49.32) * mm});
            skPoint(sketch, "E51.0.1.6", {"position": v(-41.44, 29.32) * mm});
            skPoint(sketch, "E51.0.1.7", {"position": v(-41.44, 9.32) * mm});
            skPoint(sketch, "E51.0.2.5", {"position": v(-31.44, 49.32) * mm});
            skPoint(sketch, "E51.0.2.6", {"position": v(-31.44, 29.32) * mm});
            skPoint(sketch, "E51.0.2.7", {"position": v(-31.44, 9.32) * mm});
            skPoint(sketch, "E51.0.3.5", {"position": v(-21.44, 49.32) * mm});
            skPoint(sketch, "E51.0.3.6", {"position": v(-21.44, 29.32) * mm});
            skPoint(sketch, "E51.0.3.7", {"position": v(-21.44, 9.32) * mm});
            skPoint(sketch, "E51.0.4.5", {"position": v(-11.44, 49.32) * mm});
            skPoint(sketch, "E51.0.4.6", {"position": v(-11.44, 29.32) * mm});
            skPoint(sketch, "E51.0.4.7", {"position": v(-11.44, 9.32) * mm});
            skPoint(sketch, "E51.0.5.5", {"position": v(-1.44, 49.32) * mm});
            skPoint(sketch, "E51.0.5.6", {"position": v(-1.44, 29.32) * mm});
            skPoint(sketch, "E51.0.5.7", {"position": v(-1.44, 9.32) * mm});
            skPoint(sketch, "E51.0.6.5", {"position": v(8.56, 49.32) * mm});
            skPoint(sketch, "E51.0.6.6", {"position": v(8.56, 29.32) * mm});
            skPoint(sketch, "E51.0.6.7", {"position": v(8.56, 9.32) * mm});
            skPoint(sketch, "E51.0.7.5", {"position": v(18.56, 49.32) * mm});
            skPoint(sketch, "E51.0.7.6", {"position": v(18.56, 29.32) * mm});
            skPoint(sketch, "E51.0.7.7", {"position": v(18.56, 9.32) * mm});
            skPoint(sketch, "E51.0.8.5", {"position": v(28.56, 49.32) * mm});
            skPoint(sketch, "E51.0.8.6", {"position": v(28.56, 29.32) * mm});
            skPoint(sketch, "E51.0.8.7", {"position": v(28.56, 9.32) * mm});
            skPoint(sketch, "E51.0.9.5", {"position": v(38.56, 49.32) * mm});
            skPoint(sketch, "E51.0.9.6", {"position": v(38.56, 29.32) * mm});
            skPoint(sketch, "E51.0.9.7", {"position": v(38.56, 9.32) * mm});
            skPoint(sketch, "E52.0.10.0", {"position": v(48.56, 149.32) * mm});
            skPoint(sketch, "E52.0.10.1", {"position": v(48.56, 129.32) * mm});
            skPoint(sketch, "E52.0.10.2", {"position": v(48.56, 109.32) * mm});
            skPoint(sketch, "E52.0.10.3", {"position": v(48.56, 89.32) * mm});
            skPoint(sketch, "E52.0.10.4", {"position": v(48.56, 69.32) * mm});
            skPoint(sketch, "E52.0.10.5", {"position": v(48.56, 49.32) * mm});
            skPoint(sketch, "E52.0.10.6", {"position": v(48.56, 29.32) * mm});
            skPoint(sketch, "E52.0.10.7", {"position": v(48.56, 9.32) * mm});
            skSolve(sketch);
        }
        {
            var Q0;
            Q0=sQuery(id+"F14.wireOp",VERTEX,"E51.0.6.5");
            var Q1;
            Q1=sQuery(id+"F14.wireOp",VERTEX,"E51.0.4.5");
            var Q2;
            Q2=sQuery(id+"F14.wireOp",VERTEX,"E51.0.7.6");
            var Q3;
            Q3=sQuery(id+"F14.wireOp",VERTEX,"E50.5.4.0");
            var Q4;
            Q4=sQuery(id+"F14.wireOp",VERTEX,"E51.0.4.7");
            var Q5;
            Q5=sQuery(id+"F14.wireOp",VERTEX,"E50.3.1.0");
            var Q6;
            Q6=sQuery(id+"F14.wireOp",VERTEX,"E51.0.0.5");
            var Q7;
            Q7=sQuery(id+"F14.wireOp",VERTEX,"E50.4.2.0");
            var Q8;
            Q8=sQuery(id+"F14.wireOp",VERTEX,"E50.4.4.0");
            var Q9;
            Q9=sQuery(id+"F14.wireOp",VERTEX,"E51.0.7.7");
            var Q10;
            Q10=sQuery(id+"F14.wireOp",VERTEX,"E50.7.0.0");
            var Q11;
            Q11=sQuery(id+"F14.wireOp",VERTEX,"E50.5.2.0");
            var Q12;
            Q12=sQuery(id+"F14.wireOp",VERTEX,"E50.9.0.0");
            var Q13;
            Q13=sQuery(id+"F14.wireOp",VERTEX,"E51.0.8.6");
            var Q14;
            Q14=sQuery(id+"F14.wireOp",VERTEX,"E51.0.1.7");
            var Q15;
            Q15=sQuery(id+"F14.wireOp",VERTEX,"E52.0.10.4");
            var Q16;
            Q16=sQuery(id+"F14.wireOp",VERTEX,"E50.3.2.0");
            var Q17;
            Q17=sQuery(id+"F14.wireOp",VERTEX,"E50.9.2.0");
            var Q18;
            Q18=sQuery(id+"F14.wireOp",VERTEX,"E50.0.4.0");
            var Q19;
            Q19=sQuery(id+"F14.wireOp",VERTEX,"E51.0.4.6");
            var Q20;
            Q20=sQuery(id+"F14.wireOp",VERTEX,"E51.0.3.6");
            var Q21;
            Q21=sQuery(id+"F14.wireOp",VERTEX,"E51.0.9.5");
            var Q22;
            Q22=sQuery(id+"F14.wireOp",VERTEX,"E52.0.10.3");
            var Q23;
            Q23=sQuery(id+"F14.wireOp",VERTEX,"E50.7.4.0");
            var Q24;
            Q24=sQuery(id+"F14.wireOp",VERTEX,"E52.0.10.1");
            var Q25;
            Q25=sQuery(id+"F14.wireOp",VERTEX,"E51.0.1.5");
            var Q26;
            Q26=sQuery(id+"F14.wireOp",VERTEX,"E50.3.3.0");
            var Q27;
            Q27=sQuery(id+"F14.wireOp",VERTEX,"E50.8.0.0");
            var Q28;
            Q28=sQuery(id+"F14.wireOp",VERTEX,"E50.7.3.0");
            var Q29;
            Q29=sQuery(id+"F14.wireOp",VERTEX,"E50.5.3.0");
            var Q30;
            Q30=sQuery(id+"F14.wireOp",VERTEX,"E52.0.10.5");
            var Q31;
            Q31=sQuery(id+"F14.wireOp",VERTEX,"E51.0.3.7");
            var Q32;
            Q32=sQuery(id+"F14.wireOp",VERTEX,"E50.0.2.0");
            var Q33;
            Q33=sQuery(id+"F14.wireOp",VERTEX,"E51.0.0.6");
            var Q34;
            Q34=sQuery(id+"F14.wireOp",VERTEX,"E51.0.5.7");
            var Q35;
            Q35=sQuery(id+"F14.wireOp",VERTEX,"E50.8.3.0");
            var Q36;
            Q36=sQuery(id+"F14.wireOp",VERTEX,"E50.1.4.0");
            var Q37;
            Q37=sQuery(id+"F14.wireOp",VERTEX,"E51.0.5.6");
            var Q38;
            Q38=sQuery(id+"F14.wireOp",VERTEX,"E50.8.1.0");
            var Q39;
            Q39=sQuery(id+"F14.wireOp",VERTEX,"E50.0.1.0");
            var Q40;
            Q40=sQuery(id+"F14.wireOp",VERTEX,"E50.6.2.0");
            var Q41;
            Q41=sQuery(id+"F14.wireOp",VERTEX,"E50.1.3.0");
            var Q42;
            Q42=sQuery(id+"F14.wireOp",VERTEX,"E51.0.8.5");
            var Q43;
            Q43=sQuery(id+"F14.wireOp",VERTEX,"E50.9.4.0");
            var Q44;
            Q44=sQuery(id+"F14.wireOp",VERTEX,"E50.7.1.0");
            var Q45;
            Q45=sQuery(id+"F14.wireOp",VERTEX,"E50.2.3.0");
            var Q46;
            Q46=sQuery(id+"F14.wireOp",VERTEX,"E51.0.8.7");
            var Q47;
            Q47=sQuery(id+"F14.wireOp",VERTEX,"E51.0.1.6");
            var Q48;
            Q48=sQuery(id+"F14.wireOp",VERTEX,"E50.2.1.0");
            var Q49;
            Q49=sQuery(id+"F14.wireOp",VERTEX,"E50.1.2.0");
            var Q50;
            Q50=sQuery(id+"F14.wireOp",VERTEX,"E52.0.10.0");
            var Q51;
            Q51=sQuery(id+"F14.wireOp",VERTEX,"E49");
            var Q52;
            Q52=sQuery(id+"F14.wireOp",VERTEX,"E51.0.2.5");
            var Q53;
            Q53=sQuery(id+"F14.wireOp",VERTEX,"E51.0.2.7");
            var Q54;
            Q54=sQuery(id+"F14.wireOp",VERTEX,"E50.9.3.0");
            var Q55;
            Q55=sQuery(id+"F14.wireOp",VERTEX,"E52.0.10.7");
            var Q56;
            Q56=sQuery(id+"F14.wireOp",VERTEX,"E51.0.0.7");
            var Q57;
            Q57=sQuery(id+"F14.wireOp",VERTEX,"E51.0.6.7");
            var Q58;
            Q58=sQuery(id+"F14.wireOp",VERTEX,"E51.0.5.5");
            var Q59;
            Q59=sQuery(id+"F14.wireOp",VERTEX,"E50.direction1.end");
            var Q60;
            Q60=sQuery(id+"F14.wireOp",VERTEX,"E52.0.10.6");
            var Q61;
            Q61=sQuery(id+"F14.wireOp",VERTEX,"E50.5.0.0");
            var Q62;
            Q62=sQuery(id+"F14.wireOp",VERTEX,"E50.4.3.0");
            var Q63;
            Q63=sQuery(id+"F14.wireOp",VERTEX,"E51.0.7.5");
            var Q64;
            Q64=sQuery(id+"F14.wireOp",VERTEX,"E50.3.4.0");
            var Q65;
            Q65=sQuery(id+"F14.wireOp",VERTEX,"E50.6.3.0");
            var Q66;
            Q66=sQuery(id+"F14.wireOp",VERTEX,"E50.8.2.0");
            var Q67;
            Q67=sQuery(id+"F14.wireOp",VERTEX,"E51.0.6.6");
            var Q68;
            Q68=sQuery(id+"F14.wireOp",VERTEX,"E50.2.0.0");
            var Q69;
            Q69=sQuery(id+"F14.wireOp",VERTEX,"E50.3.0.0");
            var Q70;
            Q70=sQuery(id+"F14.wireOp",VERTEX,"E50.5.1.0");
            var Q71;
            Q71=sQuery(id+"F14.wireOp",VERTEX,"E50.9.1.0");
            var Q72;
            Q72=sQuery(id+"F14.wireOp",VERTEX,"E50.6.0.0");
            var Q73;
            Q73=sQuery(id+"F14.wireOp",VERTEX,"E50.7.2.0");
            var Q74;
            Q74=sQuery(id+"F14.wireOp",VERTEX,"E51.0.3.5");
            var Q75;
            Q75=sQuery(id+"F14.wireOp",VERTEX,"E51.0.9.6");
            var Q76;
            Q76=sQuery(id+"F14.wireOp",VERTEX,"E51.0.9.7");
            var Q77;
            Q77=sQuery(id+"F14.wireOp",VERTEX,"E50.2.2.0");
            var Q78;
            Q78=sQuery(id+"F14.wireOp",VERTEX,"E50.0.3.0");
            var Q79;
            Q79=sQuery(id+"F14.wireOp",VERTEX,"E50.6.4.0");
            var Q80;
            Q80=sQuery(id+"F14.wireOp",VERTEX,"E50.8.4.0");
            var Q81;
            Q81=sQuery(id+"F14.wireOp",VERTEX,"E50.6.1.0");
            var Q82;
            Q82=sQuery(id+"F14.wireOp",VERTEX,"E52.0.10.2");
            var Q83;
            Q83=sQuery(id+"F14.wireOp",VERTEX,"E51.0.2.6");
            var Q84;
            Q84=sQuery(id+"F14.wireOp",VERTEX,"E50.4.1.0");
            var Q85;
            Q85=sQuery(id+"F14.wireOp",VERTEX,"E50.2.4.0");
            var Q86;
            Q86=sQuery(id+"F14.wireOp",VERTEX,"E50.4.0.0");
            var Q87;
            Q87=sQuery(id+"F14.wireOp",VERTEX,"E50.1.1.0");
            var Q88;
            Q88=makeQuery(id+"F5.opLoft","SWEPT_BODY",BODY,{"disambiguationData":[OSD([makeQuery(id+"F1.imprint","IMPRINT",FACE,{"disambiguationData":[TD([[makeQuery(id+"F1.imprint","IMPRINT",EDGE,{"derivedFrom":sQuery(id+"F1.wireOp",EDGE,"E0.bottom")}),-1.0]])]}),makeQuery(id+"F2.imprint","IMPRINT",FACE,{"disambiguationData":[TD([[makeQuery(id+"F2.imprint","IMPRINT",EDGE,{"derivedFrom":sQuery(id+"F2.wireOp",EDGE,"E5.bottom")}),-1.0]])]})])]});
            hole(context, id + "F15", {"style" : HoleStyle.SIMPLE, "endStyle" : HoleEndStyle.BLIND, "holeDiameter" : 1 * mm, "holeDepth" : 1 * mm, "tappedDepth" : 12 * mm, "tapClearance" : 3, "locations" : qUnion([Q0, Q1, Q2, Q3, Q4, Q5, Q6, Q7, Q8, Q9, Q10, Q11, Q12, Q13, Q14, Q15, Q16, Q17, Q18, Q19, Q20, Q21, Q22, Q23, Q24, Q25, Q26, Q27, Q28, Q29, Q30, Q31, Q32, Q33, Q34, Q35, Q36, Q37, Q38, Q39, Q40, Q41, Q42, Q43, Q44, Q45, Q46, Q47, Q48, Q49, Q50, Q51, Q52, Q53, Q54, Q55, Q56, Q57, Q58, Q59, Q60, Q61, Q62, Q63, Q64, Q65, Q66, Q67, Q68, Q69, Q70, Q71, Q72, Q73, Q74, Q75, Q76, Q77, Q78, Q79, Q80, Q81, Q82, Q83, Q84, Q85, Q86, Q87]), "scope" : qUnion([Q88])});
        }
        {
            var Q0;
            Q0=sQuery(id+"F11.wireOp",VERTEX,"E46.0.1.6");
            var Q1;
            Q1=sQuery(id+"F11.wireOp",VERTEX,"E46.0.8.6");
            var Q2;
            Q2=sQuery(id+"F11.wireOp",VERTEX,"E46.0.1.5");
            var Q3;
            Q3=sQuery(id+"F11.wireOp",VERTEX,"E45.direction2.end");
            var Q4;
            Q4=sQuery(id+"F11.wireOp",VERTEX,"E45.4.2.0");
            var Q5;
            Q5=sQuery(id+"F11.wireOp",VERTEX,"E45.9.4.0");
            var Q6;
            Q6=sQuery(id+"F11.wireOp",VERTEX,"E45.7.1.0");
            var Q7;
            Q7=sQuery(id+"F11.wireOp",VERTEX,"E46.0.6.5");
            var Q8;
            Q8=sQuery(id+"F11.wireOp",VERTEX,"E45.2.0.0");
            var Q9;
            Q9=sQuery(id+"F11.wireOp",VERTEX,"E45.7.0.0");
            var Q10;
            Q10=sQuery(id+"F11.wireOp",VERTEX,"E45.4.1.0");
            var Q11;
            Q11=sQuery(id+"F11.wireOp",VERTEX,"E46.0.6.7");
            var Q12;
            Q12=sQuery(id+"F11.wireOp",VERTEX,"E46.0.7.5");
            var Q13;
            Q13=sQuery(id+"F11.wireOp",VERTEX,"E46.0.8.5");
            var Q14;
            Q14=sQuery(id+"F11.wireOp",VERTEX,"E46.0.9.7");
            var Q15;
            Q15=sQuery(id+"F11.wireOp",VERTEX,"E46.0.5.7");
            var Q16;
            Q16=sQuery(id+"F11.wireOp",VERTEX,"E45.9.1.0");
            var Q17;
            Q17=sQuery(id+"F11.wireOp",VERTEX,"E47.0.10.1");
            var Q18;
            Q18=sQuery(id+"F11.wireOp",VERTEX,"E45.5.3.0");
            var Q19;
            Q19=sQuery(id+"F11.wireOp",VERTEX,"E46.0.5.5");
            var Q20;
            Q20=sQuery(id+"F11.wireOp",VERTEX,"E45.3.4.0");
            var Q21;
            Q21=sQuery(id+"F11.wireOp",VERTEX,"E46.0.4.7");
            var Q22;
            Q22=sQuery(id+"F11.wireOp",VERTEX,"E45.2.3.0");
            var Q23;
            Q23=sQuery(id+"F11.wireOp",VERTEX,"E46.0.3.7");
            var Q24;
            Q24=sQuery(id+"F11.wireOp",VERTEX,"E47.0.10.6");
            var Q25;
            Q25=sQuery(id+"F11.wireOp",VERTEX,"E46.0.9.5");
            var Q26;
            Q26=sQuery(id+"F11.wireOp",VERTEX,"E45.4.0.0");
            var Q27;
            Q27=sQuery(id+"F11.wireOp",VERTEX,"E45.3.1.0");
            var Q28;
            Q28=sQuery(id+"F11.wireOp",VERTEX,"E45.9.2.0");
            var Q29;
            Q29=sQuery(id+"F11.wireOp",VERTEX,"E46.0.2.5");
            var Q30;
            Q30=sQuery(id+"F11.wireOp",VERTEX,"E46.0.2.7");
            var Q31;
            Q31=sQuery(id+"F11.wireOp",VERTEX,"E45.0.2.0");
            var Q32;
            Q32=sQuery(id+"F11.wireOp",VERTEX,"E44");
            var Q33;
            Q33=sQuery(id+"F11.wireOp",VERTEX,"E45.3.0.0");
            var Q34;
            Q34=sQuery(id+"F11.wireOp",VERTEX,"E46.0.4.6");
            var Q35;
            Q35=sQuery(id+"F11.wireOp",VERTEX,"E45.2.1.0");
            var Q36;
            Q36=sQuery(id+"F11.wireOp",VERTEX,"E45.5.0.0");
            var Q37;
            Q37=sQuery(id+"F11.wireOp",VERTEX,"E45.4.3.0");
            var Q38;
            Q38=sQuery(id+"F11.wireOp",VERTEX,"E45.5.4.0");
            var Q39;
            Q39=sQuery(id+"F11.wireOp",VERTEX,"E45.6.3.0");
            var Q40;
            Q40=sQuery(id+"F11.wireOp",VERTEX,"E45.7.2.0");
            var Q41;
            Q41=sQuery(id+"F11.wireOp",VERTEX,"E47.0.10.2");
            var Q42;
            Q42=sQuery(id+"F11.wireOp",VERTEX,"E45.7.3.0");
            var Q43;
            Q43=sQuery(id+"F11.wireOp",VERTEX,"E45.6.1.0");
            var Q44;
            Q44=sQuery(id+"F11.wireOp",VERTEX,"E46.0.1.7");
            var Q45;
            Q45=sQuery(id+"F11.wireOp",VERTEX,"E45.2.4.0");
            var Q46;
            Q46=sQuery(id+"F11.wireOp",VERTEX,"E46.0.7.7");
            var Q47;
            Q47=sQuery(id+"F11.wireOp",VERTEX,"E47.0.10.3");
            var Q48;
            Q48=sQuery(id+"F11.wireOp",VERTEX,"E45.3.3.0");
            var Q49;
            Q49=sQuery(id+"F11.wireOp",VERTEX,"E45.7.4.0");
            var Q50;
            Q50=sQuery(id+"F11.wireOp",VERTEX,"E46.0.9.6");
            var Q51;
            Q51=sQuery(id+"F11.wireOp",VERTEX,"E45.8.0.0");
            var Q52;
            Q52=sQuery(id+"F11.wireOp",VERTEX,"E45.1.4.0");
            var Q53;
            Q53=sQuery(id+"F11.wireOp",VERTEX,"E46.0.6.6");
            var Q54;
            Q54=sQuery(id+"F11.wireOp",VERTEX,"E47.0.10.5");
            var Q55;
            Q55=sQuery(id+"F11.wireOp",VERTEX,"E46.0.3.6");
            var Q56;
            Q56=sQuery(id+"F11.wireOp",VERTEX,"E45.9.0.0");
            var Q57;
            Q57=sQuery(id+"F11.wireOp",VERTEX,"E45.direction1.end");
            var Q58;
            Q58=sQuery(id+"F11.wireOp",VERTEX,"E46.0.0.5");
            var Q59;
            Q59=sQuery(id+"F11.wireOp",VERTEX,"E47.0.10.7");
            var Q60;
            Q60=sQuery(id+"F11.wireOp",VERTEX,"E45.0.4.0");
            var Q61;
            Q61=sQuery(id+"F11.wireOp",VERTEX,"E45.0.3.0");
            var Q62;
            Q62=sQuery(id+"F11.wireOp",VERTEX,"E46.0.0.6");
            var Q63;
            Q63=sQuery(id+"F11.wireOp",VERTEX,"E45.6.2.0");
            var Q64;
            Q64=sQuery(id+"F11.wireOp",VERTEX,"E45.3.2.0");
            var Q65;
            Q65=sQuery(id+"F11.wireOp",VERTEX,"E45.9.3.0");
            var Q66;
            Q66=sQuery(id+"F11.wireOp",VERTEX,"E46.0.3.5");
            var Q67;
            Q67=sQuery(id+"F11.wireOp",VERTEX,"E45.5.2.0");
            var Q68;
            Q68=sQuery(id+"F11.wireOp",VERTEX,"E46.0.4.5");
            var Q69;
            Q69=sQuery(id+"F11.wireOp",VERTEX,"E45.6.0.0");
            var Q70;
            Q70=sQuery(id+"F11.wireOp",VERTEX,"E46.0.0.7");
            var Q71;
            Q71=sQuery(id+"F11.wireOp",VERTEX,"E45.8.3.0");
            var Q72;
            Q72=sQuery(id+"F11.wireOp",VERTEX,"E47.0.10.4");
            var Q73;
            Q73=sQuery(id+"F11.wireOp",VERTEX,"E45.2.2.0");
            var Q74;
            Q74=sQuery(id+"F11.wireOp",VERTEX,"E46.0.8.7");
            var Q75;
            Q75=sQuery(id+"F11.wireOp",VERTEX,"E46.0.2.6");
            var Q76;
            Q76=sQuery(id+"F11.wireOp",VERTEX,"E45.5.1.0");
            var Q77;
            Q77=sQuery(id+"F11.wireOp",VERTEX,"E45.8.1.0");
            var Q78;
            Q78=sQuery(id+"F11.wireOp",VERTEX,"E46.0.7.6");
            var Q79;
            Q79=sQuery(id+"F11.wireOp",VERTEX,"E45.4.4.0");
            var Q80;
            Q80=sQuery(id+"F11.wireOp",VERTEX,"E45.8.2.0");
            var Q81;
            Q81=sQuery(id+"F11.wireOp",VERTEX,"E45.1.1.0");
            var Q82;
            Q82=sQuery(id+"F11.wireOp",VERTEX,"E47.0.10.0");
            var Q83;
            Q83=sQuery(id+"F11.wireOp",VERTEX,"E45.6.4.0");
            var Q84;
            Q84=sQuery(id+"F11.wireOp",VERTEX,"E46.0.5.6");
            var Q85;
            Q85=sQuery(id+"F11.wireOp",VERTEX,"E45.1.3.0");
            var Q86;
            Q86=sQuery(id+"F11.wireOp",VERTEX,"E45.1.2.0");
            var Q87;
            Q87=sQuery(id+"F11.wireOp",VERTEX,"E45.8.4.0");
            var Q88;
            Q88=makeQuery(id+"F5.opLoft","SWEPT_BODY",BODY,{"disambiguationData":[OSD([makeQuery(id+"F1.imprint","IMPRINT",FACE,{"disambiguationData":[TD([[makeQuery(id+"F1.imprint","IMPRINT",EDGE,{"derivedFrom":sQuery(id+"F1.wireOp",EDGE,"E0.bottom")}),-1.0]])]}),makeQuery(id+"F2.imprint","IMPRINT",FACE,{"disambiguationData":[TD([[makeQuery(id+"F2.imprint","IMPRINT",EDGE,{"derivedFrom":sQuery(id+"F2.wireOp",EDGE,"E5.bottom")}),-1.0]])]})])]});
            hole(context, id + "F16", {"style" : HoleStyle.SIMPLE, "endStyle" : HoleEndStyle.BLIND, "holeDiameter" : 1 * mm, "holeDepth" : 1 * mm, "tappedDepth" : 12 * mm, "tapClearance" : 3, "locations" : qUnion([Q0, Q1, Q2, Q3, Q4, Q5, Q6, Q7, Q8, Q9, Q10, Q11, Q12, Q13, Q14, Q15, Q16, Q17, Q18, Q19, Q20, Q21, Q22, Q23, Q24, Q25, Q26, Q27, Q28, Q29, Q30, Q31, Q32, Q33, Q34, Q35, Q36, Q37, Q38, Q39, Q40, Q41, Q42, Q43, Q44, Q45, Q46, Q47, Q48, Q49, Q50, Q51, Q52, Q53, Q54, Q55, Q56, Q57, Q58, Q59, Q60, Q61, Q62, Q63, Q64, Q65, Q66, Q67, Q68, Q69, Q70, Q71, Q72, Q73, Q74, Q75, Q76, Q77, Q78, Q79, Q80, Q81, Q82, Q83, Q84, Q85, Q86, Q87]), "scope" : qUnion([Q88])});
        }
        {
            var Q0;
            Q0=sQuery(id+"F10.wireOp",VERTEX,"E43.0.10.0");
            var Q1;
            Q1=sQuery(id+"F10.wireOp",VERTEX,"E42.0.2.7");
            var Q2;
            Q2=sQuery(id+"F10.wireOp",VERTEX,"E42.0.6.5");
            var Q3;
            Q3=sQuery(id+"F10.wireOp",VERTEX,"E42.0.7.6");
            var Q4;
            Q4=sQuery(id+"F10.wireOp",VERTEX,"E41.6.3.0");
            var Q5;
            Q5=sQuery(id+"F10.wireOp",VERTEX,"E41.3.1.0");
            var Q6;
            Q6=sQuery(id+"F10.wireOp",VERTEX,"E41.7.2.0");
            var Q7;
            Q7=sQuery(id+"F10.wireOp",VERTEX,"E41.9.3.0");
            var Q8;
            Q8=sQuery(id+"F10.wireOp",VERTEX,"E41.1.4.0");
            var Q9;
            Q9=sQuery(id+"F10.wireOp",VERTEX,"E41.0.1.0");
            var Q10;
            Q10=sQuery(id+"F10.wireOp",VERTEX,"E41.9.1.0");
            var Q11;
            Q11=sQuery(id+"F10.wireOp",VERTEX,"E41.8.1.0");
            var Q12;
            Q12=sQuery(id+"F10.wireOp",VERTEX,"E43.0.10.5");
            var Q13;
            Q13=sQuery(id+"F10.wireOp",VERTEX,"E43.0.10.7");
            var Q14;
            Q14=sQuery(id+"F10.wireOp",VERTEX,"E41.5.4.0");
            var Q15;
            Q15=sQuery(id+"F10.wireOp",VERTEX,"E42.0.2.5");
            var Q16;
            Q16=sQuery(id+"F10.wireOp",VERTEX,"E42.0.5.5");
            var Q17;
            Q17=sQuery(id+"F10.wireOp",VERTEX,"E42.0.8.7");
            var Q18;
            Q18=sQuery(id+"F10.wireOp",VERTEX,"E42.0.3.5");
            var Q19;
            Q19=sQuery(id+"F10.wireOp",VERTEX,"E42.0.8.6");
            var Q20;
            Q20=sQuery(id+"F10.wireOp",VERTEX,"E41.2.0.0");
            var Q21;
            Q21=sQuery(id+"F10.wireOp",VERTEX,"E41.8.4.0");
            var Q22;
            Q22=sQuery(id+"F10.wireOp",VERTEX,"E41.3.2.0");
            var Q23;
            Q23=sQuery(id+"F10.wireOp",VERTEX,"E41.2.2.0");
            var Q24;
            Q24=sQuery(id+"F10.wireOp",VERTEX,"E41.4.0.0");
            var Q25;
            Q25=sQuery(id+"F10.wireOp",VERTEX,"E43.0.10.4");
            var Q26;
            Q26=sQuery(id+"F10.wireOp",VERTEX,"E42.0.4.5");
            var Q27;
            Q27=sQuery(id+"F10.wireOp",VERTEX,"E41.1.0.0");
            var Q28;
            Q28=sQuery(id+"F10.wireOp",VERTEX,"E41.5.1.0");
            var Q29;
            Q29=sQuery(id+"F10.wireOp",VERTEX,"E41.1.3.0");
            var Q30;
            Q30=sQuery(id+"F10.wireOp",VERTEX,"E41.0.4.0");
            var Q31;
            Q31=sQuery(id+"F10.wireOp",VERTEX,"E41.9.4.0");
            var Q32;
            Q32=sQuery(id+"F10.wireOp",VERTEX,"E41.7.1.0");
            var Q33;
            Q33=sQuery(id+"F10.wireOp",VERTEX,"E42.0.4.7");
            var Q34;
            Q34=sQuery(id+"F10.wireOp",VERTEX,"E41.4.3.0");
            var Q35;
            Q35=sQuery(id+"F10.wireOp",VERTEX,"E41.3.4.0");
            var Q36;
            Q36=sQuery(id+"F10.wireOp",VERTEX,"E41.1.1.0");
            var Q37;
            Q37=sQuery(id+"F10.wireOp",VERTEX,"E42.0.5.6");
            var Q38;
            Q38=sQuery(id+"F10.wireOp",VERTEX,"E41.4.4.0");
            var Q39;
            Q39=sQuery(id+"F10.wireOp",VERTEX,"E42.0.3.6");
            var Q40;
            Q40=sQuery(id+"F10.wireOp",VERTEX,"E42.0.0.6");
            var Q41;
            Q41=sQuery(id+"F10.wireOp",VERTEX,"E42.0.7.5");
            var Q42;
            Q42=sQuery(id+"F10.wireOp",VERTEX,"E42.0.0.5");
            var Q43;
            Q43=sQuery(id+"F10.wireOp",VERTEX,"E41.8.2.0");
            var Q44;
            Q44=sQuery(id+"F10.wireOp",VERTEX,"E42.0.0.7");
            var Q45;
            Q45=sQuery(id+"F10.wireOp",VERTEX,"E42.0.1.7");
            var Q46;
            Q46=sQuery(id+"F10.wireOp",VERTEX,"E42.0.2.6");
            var Q47;
            Q47=sQuery(id+"F10.wireOp",VERTEX,"E42.0.3.7");
            var Q48;
            Q48=sQuery(id+"F10.wireOp",VERTEX,"E41.7.0.0");
            var Q49;
            Q49=sQuery(id+"F10.wireOp",VERTEX,"E41.0.3.0");
            var Q50;
            Q50=sQuery(id+"F10.wireOp",VERTEX,"E41.5.0.0");
            var Q51;
            Q51=sQuery(id+"F10.wireOp",VERTEX,"E41.6.0.0");
            var Q52;
            Q52=sQuery(id+"F10.wireOp",VERTEX,"E42.0.7.7");
            var Q53;
            Q53=sQuery(id+"F10.wireOp",VERTEX,"E43.0.10.2");
            var Q54;
            Q54=sQuery(id+"F10.wireOp",VERTEX,"E41.4.1.0");
            var Q55;
            Q55=sQuery(id+"F10.wireOp",VERTEX,"E40");
            var Q56;
            Q56=sQuery(id+"F10.wireOp",VERTEX,"E42.0.5.7");
            var Q57;
            Q57=sQuery(id+"F10.wireOp",VERTEX,"E41.7.4.0");
            var Q58;
            Q58=sQuery(id+"F10.wireOp",VERTEX,"E42.0.9.6");
            var Q59;
            Q59=sQuery(id+"F10.wireOp",VERTEX,"E41.0.2.0");
            var Q60;
            Q60=sQuery(id+"F10.wireOp",VERTEX,"E42.0.8.5");
            var Q61;
            Q61=sQuery(id+"F10.wireOp",VERTEX,"E41.5.3.0");
            var Q62;
            Q62=sQuery(id+"F10.wireOp",VERTEX,"E42.0.9.5");
            var Q63;
            Q63=sQuery(id+"F10.wireOp",VERTEX,"E43.0.10.3");
            var Q64;
            Q64=sQuery(id+"F10.wireOp",VERTEX,"E41.8.3.0");
            var Q65;
            Q65=sQuery(id+"F10.wireOp",VERTEX,"E41.5.2.0");
            var Q66;
            Q66=sQuery(id+"F10.wireOp",VERTEX,"E41.9.0.0");
            var Q67;
            Q67=sQuery(id+"F10.wireOp",VERTEX,"E41.3.3.0");
            var Q68;
            Q68=sQuery(id+"F10.wireOp",VERTEX,"E41.2.1.0");
            var Q69;
            Q69=sQuery(id+"F10.wireOp",VERTEX,"E41.2.4.0");
            var Q70;
            Q70=sQuery(id+"F10.wireOp",VERTEX,"E42.0.6.6");
            var Q71;
            Q71=sQuery(id+"F10.wireOp",VERTEX,"E41.1.2.0");
            var Q72;
            Q72=sQuery(id+"F10.wireOp",VERTEX,"E41.8.0.0");
            var Q73;
            Q73=sQuery(id+"F10.wireOp",VERTEX,"E42.0.1.5");
            var Q74;
            Q74=sQuery(id+"F10.wireOp",VERTEX,"E43.0.10.6");
            var Q75;
            Q75=sQuery(id+"F10.wireOp",VERTEX,"E41.2.3.0");
            var Q76;
            Q76=sQuery(id+"F10.wireOp",VERTEX,"E41.6.2.0");
            var Q77;
            Q77=sQuery(id+"F10.wireOp",VERTEX,"E41.6.4.0");
            var Q78;
            Q78=sQuery(id+"F10.wireOp",VERTEX,"E43.0.10.1");
            var Q79;
            Q79=sQuery(id+"F10.wireOp",VERTEX,"E42.0.6.7");
            var Q80;
            Q80=sQuery(id+"F10.wireOp",VERTEX,"E41.4.2.0");
            var Q81;
            Q81=sQuery(id+"F10.wireOp",VERTEX,"E42.0.1.6");
            var Q82;
            Q82=sQuery(id+"F10.wireOp",VERTEX,"E41.7.3.0");
            var Q83;
            Q83=sQuery(id+"F10.wireOp",VERTEX,"E41.9.2.0");
            var Q84;
            Q84=sQuery(id+"F10.wireOp",VERTEX,"E41.6.1.0");
            var Q85;
            Q85=sQuery(id+"F10.wireOp",VERTEX,"E42.0.9.7");
            var Q86;
            Q86=sQuery(id+"F10.wireOp",VERTEX,"E42.0.4.6");
            var Q87;
            Q87=sQuery(id+"F10.wireOp",VERTEX,"E41.3.0.0");
            var Q88;
            Q88=makeQuery(id+"F5.opLoft","SWEPT_BODY",BODY,{"disambiguationData":[OSD([makeQuery(id+"F1.imprint","IMPRINT",FACE,{"disambiguationData":[TD([[makeQuery(id+"F1.imprint","IMPRINT",EDGE,{"derivedFrom":sQuery(id+"F1.wireOp",EDGE,"E0.bottom")}),-1.0]])]}),makeQuery(id+"F2.imprint","IMPRINT",FACE,{"disambiguationData":[TD([[makeQuery(id+"F2.imprint","IMPRINT",EDGE,{"derivedFrom":sQuery(id+"F2.wireOp",EDGE,"E5.bottom")}),-1.0]])]})])]});
            hole(context, id + "F17", {"style" : HoleStyle.SIMPLE, "endStyle" : HoleEndStyle.BLIND, "holeDiameter" : 1 * mm, "holeDepth" : 1 * mm, "tappedDepth" : 12 * mm, "tapClearance" : 3, "locations" : qUnion([Q0, Q1, Q2, Q3, Q4, Q5, Q6, Q7, Q8, Q9, Q10, Q11, Q12, Q13, Q14, Q15, Q16, Q17, Q18, Q19, Q20, Q21, Q22, Q23, Q24, Q25, Q26, Q27, Q28, Q29, Q30, Q31, Q32, Q33, Q34, Q35, Q36, Q37, Q38, Q39, Q40, Q41, Q42, Q43, Q44, Q45, Q46, Q47, Q48, Q49, Q50, Q51, Q52, Q53, Q54, Q55, Q56, Q57, Q58, Q59, Q60, Q61, Q62, Q63, Q64, Q65, Q66, Q67, Q68, Q69, Q70, Q71, Q72, Q73, Q74, Q75, Q76, Q77, Q78, Q79, Q80, Q81, Q82, Q83, Q84, Q85, Q86, Q87]), "scope" : qUnion([Q88])});
        }
    });
